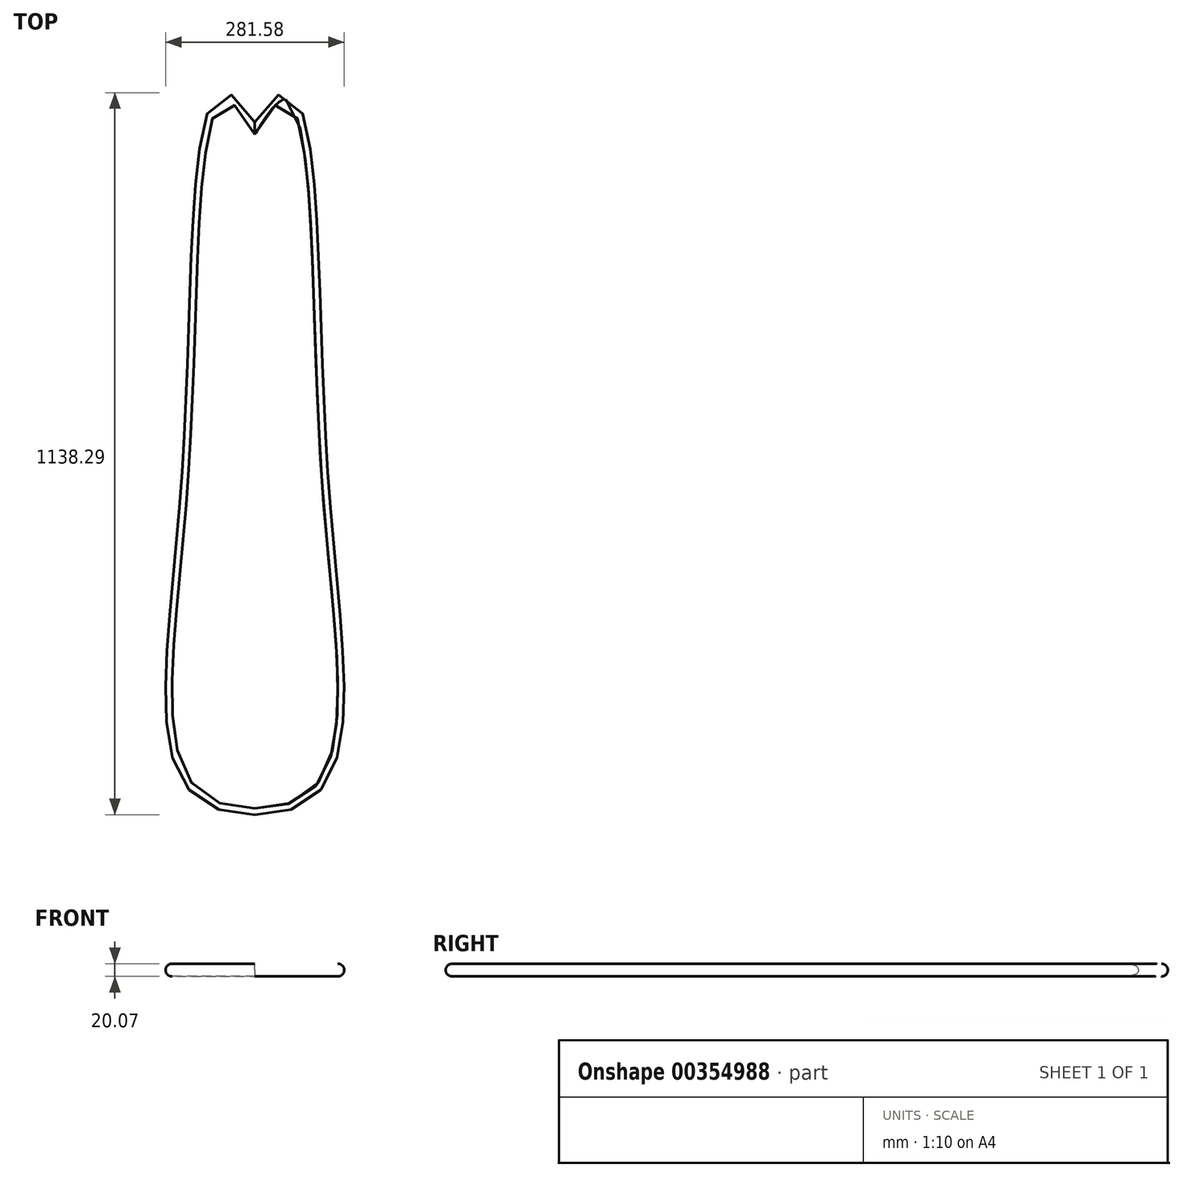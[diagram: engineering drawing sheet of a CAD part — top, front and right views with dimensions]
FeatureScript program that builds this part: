
annotation { "Feature Type Name" : "Feature", "Feature Type Description" : "" }
export const myFeature = defineFeature(function(context is Context, id is Id, definition is map)
    precondition{}
    {
        {
            var Q0;
            Q0=qCreatedBy(makeId("Top.planeOp"),FACE);
            var sketch = newSketch(context, id + "F0", { "sketchPlane" : qUnion([Q0])});
            skLineSegment(sketch, "E0", {"start": v(0, 0) * mm, "end": v(0, 546.1) * mm});
            skSolve(sketch);
        }
        {
            var Q0;
            Q0=qCreatedBy(makeId("Top.planeOp"),FACE);
            var sketch = newSketch(context, id + "F1", { "sketchPlane" : qUnion([Q0])});
            skLineSegment(sketch, "E1.bottom", {"start": v(-114.3, -546.1) * mm, "end": v(114.3, -546.1) * mm});
            skLineSegment(sketch, "E1.top", {"start": v(-114.3, 546.1) * mm, "end": v(114.3, 546.1) * mm});
            skLineSegment(sketch, "E1.left", {"start": v(-114.3, -546.1) * mm, "end": v(-114.3, 546.1) * mm});
            skLineSegment(sketch, "E1.right", {"start": v(114.3, -546.1) * mm, "end": v(114.3, 546.1) * mm});
            skPoint(sketch, "E1.middle", {"position": v(0, 0) * mm});
            skSolve(sketch);
        }
        {
            var Q0;
            Q0=makeQuery(id+"F1.imprint","IMPRINT",FACE,{"disambiguationData":[TD([[makeQuery(id+"F1.imprint","IMPRINT",EDGE,{"derivedFrom":sQuery(id+"F1.wireOp",EDGE,"E1.bottom")}),1.0]])]});
            var sketch = newSketch(context, id + "F2", { "sketchPlane" : qUnion([Q0])});
            skFitSpline(sketch, "E2", {"points": [v(0, -546.1) * mm, v(114.3, 0) * mm, v(0, 546.1) * mm], "startDerivative": vector(1192.96, -5.3) * mm, "endDerivative": vector(-686.78, -1111.08) * mm});
            skFitSpline(sketch, "E3.MirrorCS", {"points": [v(0, -546.1) * mm, v(-114.3, 0) * mm, v(0, 546.1) * mm], "startDerivative": vector(-1192.96, -5.3) * mm, "endDerivative": vector(686.78, -1111.08) * mm});
            skSolve(sketch);
        }
        {
            var Q0;
            Q0 = qSketchRegion(id + "F2", true);
            extrude(context, id + "F3", {"entities" : qUnion([Q0]), "depth" : -20.07 * mm});
        }
        {
            var Q0;
            Q0=makeQuery(id+"F3.opExtrude","CAP_EDGE",EDGE,{"disambiguationData":[OSD([sQuery(id+"F2.wireOp",EDGE,"E3.MirrorCS")])],"isStart":true});
            var Q1;
            Q1=makeQuery(id+"F3.opExtrude","CAP_EDGE",EDGE,{"disambiguationData":[OSD([sQuery(id+"F2.wireOp",EDGE,"E3.MirrorCS")])],"isStart":false});
            var Q2;
            Q2=makeQuery(id+"F3.opExtrude","CAP_EDGE",EDGE,{"disambiguationData":[OSD([sQuery(id+"F2.wireOp",EDGE,"E2")])],"isStart":true});
            var Q3;
            Q3=makeQuery(id+"F3.opExtrude","CAP_EDGE",EDGE,{"disambiguationData":[OSD([sQuery(id+"F2.wireOp",EDGE,"E2")])],"isStart":false});
            fillet(context, id + "F4", {"entities" : qUnion([Q0, Q1, Q2, Q3]), "radius" : 10.03 * mm, "tangentPropagation" : true, "allowEdgeOverflow" : false});
        }
    });
